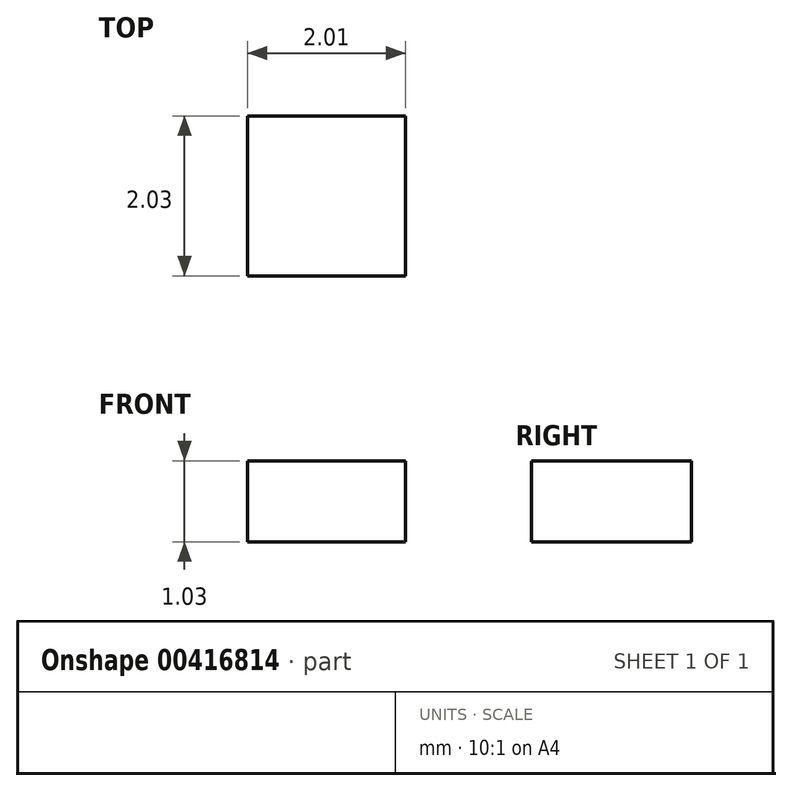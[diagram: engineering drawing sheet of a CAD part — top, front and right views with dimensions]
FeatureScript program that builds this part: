
annotation { "Feature Type Name" : "Feature", "Feature Type Description" : "" }
export const myFeature = defineFeature(function(context is Context, id is Id, definition is map)
    precondition{}
    {
        {
            var Q0;
            Q0=qCreatedBy(makeId("Top.planeOp"),FACE);
            var sketch = newSketch(context, id + "F0", { "sketchPlane" : qUnion([Q0])});
            skLineSegment(sketch, "E0.bottom", {"start": v(0, 0) * mm, "end": v(2, 0) * mm});
            skLineSegment(sketch, "E0.top", {"start": v(0, 2.03) * mm, "end": v(2, 2.03) * mm});
            skLineSegment(sketch, "E0.left", {"start": v(0, 0) * mm, "end": v(0, 2.03) * mm});
            skLineSegment(sketch, "E0.right", {"start": v(2, 0) * mm, "end": v(2, 2.03) * mm});
            skSolve(sketch);
        }
        {
            var Q0;
            Q0 = qSketchRegion(id + "F0", true);
            extrude(context, id + "F1", {"entities" : qUnion([Q0]), "depth" : 1.03 * mm, "offsetDistance" : 25.4 * mm});
        }
    });
